# Revit family: 63_UN_Lightline_WDO L650_Norton
name_source: partatom
category: Lighting Fixtures
units: mm (PartAtom-declared; Revit-internal decimal feet)

## family parameters
Always vertical = Yes
Cut with Voids When Loaded = No
Light Source = Yes
OmniClass Number = 23.80.70.11.14.11
OmniClass Title = Downlights
Part Type = Normal
Room Calculation Point = Yes
Round Connector Dimension = Use Diameter
Shared = No
Work Plane-Based = No

## types (2) — shared parameters
Assembly Code = 63.0
Bracket_Distance = 390 mm
Color Filter = 16777215
Dimming Lamp Color Temperature Shift = <None>
Emit Shape Visible in Rendering = No
Emit from Rectangle Width = 625 mm  [stored 2.05052 ft]
Housing_Material = Laminate, White
IK Value = IK08
IP Value = IP66
IfcExportAs = IfcLightFixtureType
IfcExportType = USERDEFINED
Lamp = LED
Length = 665 mm  [stored 2.18176 ft]
Manufacturer = Norton
Model = WDO
Type Comments = L600
URL = https://www.ivlibrary.com
Voltage = 230 V
calc_length = 625 mm  [stored 2.05052 ft]

## per-type parameters (varying)
| type | Apparent Load | Emit from Rectangle Length | Luminous Flux (lm) | Photometric Web File | Tilt Angle | Wattage Comments |
| WDO 84 1 1200 650 | 8 VA | 1219 mm | 1250 lm | WDO8411200650_LDT.ies | 60.00° | 8W |
| WDO 84 1 2000 650 | 16 VA | 90 mm  [stored 0.295276 ft] | 2000 lm | WDO8412000650_LDT.ies | 90.00° | 16W |

note: [stored X ft] marks values corroborated as IEEE doubles in the binary element streams (Revit-internal decimal feet)

## geometry (parser evidence)
native form markers: Sweep x5
no freeform markers — native parametric forms only
